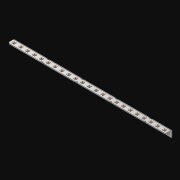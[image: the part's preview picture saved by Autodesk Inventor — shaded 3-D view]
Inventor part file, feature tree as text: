
AUTODESK INVENTOR PART (.ipt)
format: ipt  version: 2021 (Build 250183000, 183)  size: 753,152 bytes
history: native  units: in
note: dims shown in document units (in); Inventor stores cm internally (conversion verified against a paired STEP export)
features: extrude x47, other x46, sketch x3, pattern_linear x1, sheet_metal_op x1
ambient origin geometry x8: Origin, YZ Plane, XZ Plane, XY Plane, X Axis, Y Axis, Z Axis, Center Point
bodies: Solid1 (feature_tree)
feature tree (98):
  pattern_linear  "Rectangular Pattern1"  Spacing1=0.063in  [1 undecoded]
  extrude  "Extrusion1"  Depth=0.5in
  sketch  "Sketch1"  dims[d0=0.182in]
  other  "Srf1"
  sketch  "Sketch2"  dims[d1=0.063in d2=0.0in]
  other  "Srf2"
  other  "Srf3"
  other  "Srf5"
  other  "Srf7"
  other  "Srf9"
  other  "Srf11"
  other  "Srf13"
  other  "Srf15"
  other  "Srf17"
  other  "Srf19"
  other  "Srf21"
  other  "Srf23"
  other  "Srf25"
  other  "Srf27"
  other  "Srf29"
  other  "Srf31"
  other  "Srf33"
  other  "Srf35"
  other  "Srf37"
  other  "Srf39"
  other  "Srf41"
  other  "Srf43"
  other  "Srf45"
  other  "Srf4"
  other  "Srf6"
  other  "Srf8"
  other  "Srf10"
  other  "Srf12"
  other  "Srf14"
  other  "Srf16"
  other  "Srf18"
  other  "Srf20"
  other  "Srf22"
  other  "Srf24"
  other  "Srf26"
  other  "Srf28"
  other  "Srf30"
  other  "Srf32"
  other  "Srf34"
  other  "Srf36"
  other  "Srf38"
  other  "Srf40"
  other  "Srf42"
  other  "Srf44"
  other  "Srf46"
  sketch  "Sketch3"  dims[d3=0.182in d4=0.063in d5=0.0in d8=0.5in d9=6.0in d10=0.0in]
  sheet_metal_op  "Fold1"
  extrude  "ExtrusionSrf1"  Depth=6.0in TaperAngle=0.0deg
  extrude  "ExtrusionSrf2"  [1 undecoded]
  extrude  "ExtrusionSrf3"  [1 undecoded]
  extrude  "ExtrusionSrf4"  [1 undecoded]
  extrude  "ExtrusionSrf5"  [1 undecoded]
  extrude  "ExtrusionSrf6"  [1 undecoded]
  extrude  "ExtrusionSrf7"  [1 undecoded]
  extrude  "ExtrusionSrf8"  [1 undecoded]
  extrude  "ExtrusionSrf9"  [1 undecoded]
  extrude  "ExtrusionSrf10"  [1 undecoded]
  extrude  "ExtrusionSrf11"  [1 undecoded]
  extrude  "ExtrusionSrf12"  [1 undecoded]
  extrude  "ExtrusionSrf13"  [1 undecoded]
  extrude  "ExtrusionSrf14"  [1 undecoded]
  extrude  "ExtrusionSrf15"  [1 undecoded]
  extrude  "ExtrusionSrf16"  [1 undecoded]
  extrude  "ExtrusionSrf17"  [1 undecoded]
  extrude  "ExtrusionSrf18"  [1 undecoded]
  extrude  "ExtrusionSrf19"  [1 undecoded]
  extrude  "ExtrusionSrf20"  [1 undecoded]
  extrude  "ExtrusionSrf21"  [1 undecoded]
  extrude  "ExtrusionSrf22"  [1 undecoded]
  extrude  "ExtrusionSrf23"  [1 undecoded]
  extrude  "ExtrusionSrf24"  [1 undecoded]
  extrude  "ExtrusionSrf37"  [1 undecoded]
  extrude  "ExtrusionSrf38"  [1 undecoded]
  extrude  "ExtrusionSrf39"  [1 undecoded]
  extrude  "ExtrusionSrf40"  [1 undecoded]
  extrude  "ExtrusionSrf41"  [1 undecoded]
  extrude  "ExtrusionSrf42"  [1 undecoded]
  extrude  "ExtrusionSrf43"  [1 undecoded]
  extrude  "ExtrusionSrf44"  [1 undecoded]
  extrude  "ExtrusionSrf45"  [1 undecoded]
  extrude  "ExtrusionSrf46"  [1 undecoded]
  extrude  "ExtrusionSrf47"  [1 undecoded]
  extrude  "ExtrusionSrf48"  [1 undecoded]
  extrude  "ExtrusionSrf49"  [1 undecoded]
  extrude  "ExtrusionSrf50"  [1 undecoded]
  extrude  "ExtrusionSrf51"  [1 undecoded]
  extrude  "ExtrusionSrf52"  [1 undecoded]
  extrude  "ExtrusionSrf53"  [1 undecoded]
  extrude  "ExtrusionSrf54"  [1 undecoded]
  extrude  "ExtrusionSrf55"  [1 undecoded]
  extrude  "ExtrusionSrf56"  [1 undecoded]
  extrude  "ExtrusionSrf57"  [1 undecoded]
  extrude  "ExtrusionSrf58"  [1 undecoded]
note: 46 required parameter values undecoded (feature->parameter linkage not recoverable at this tier; creation-order binding heuristic only, values carry confidence <= 0.55)
